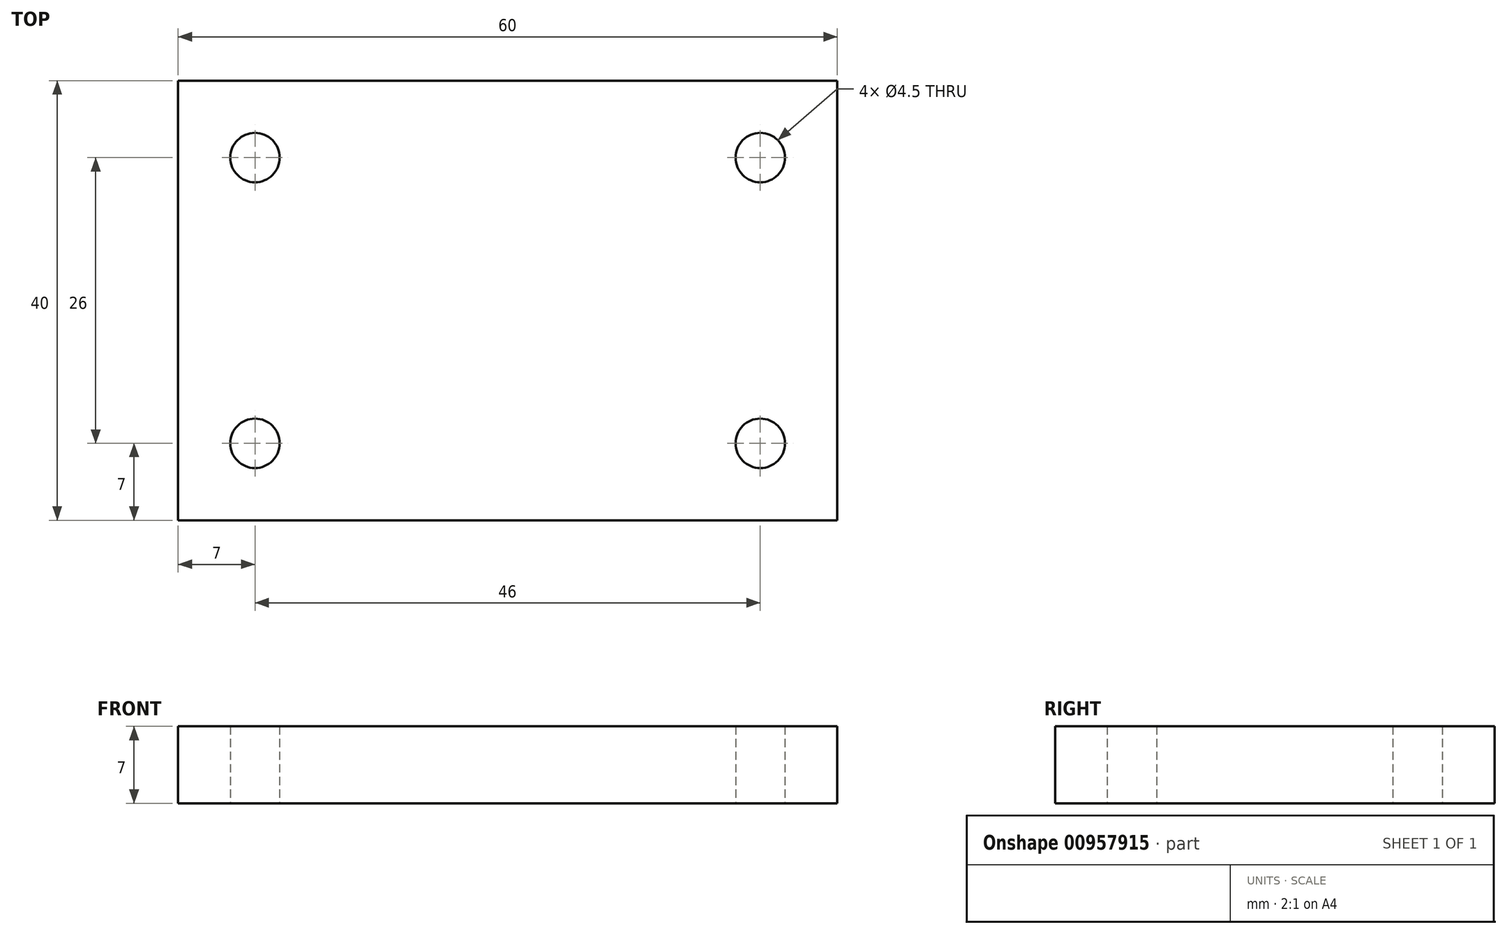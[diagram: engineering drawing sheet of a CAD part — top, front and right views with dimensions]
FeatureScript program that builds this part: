
annotation { "Feature Type Name" : "Feature", "Feature Type Description" : "" }
export const myFeature = defineFeature(function(context is Context, id is Id, definition is map)
    precondition{}
    {
        {
            var Q0;
            Q0=qCreatedBy(makeId("Top.planeOp"),FACE);
            var sketch = newSketch(context, id + "F0", { "sketchPlane" : qUnion([Q0])});
            skLineSegment(sketch, "E0.bottom", {"start": v(-30, 20) * mm, "end": v(30, 20) * mm});
            skLineSegment(sketch, "E0.top", {"start": v(-30, -20) * mm, "end": v(30, -20) * mm});
            skLineSegment(sketch, "E0.left", {"start": v(-30, 20) * mm, "end": v(-30, -20) * mm});
            skLineSegment(sketch, "E0.right", {"start": v(30, 20) * mm, "end": v(30, -20) * mm});
            skCircle(sketch, "E1", {"center": v(-23, 13) * mm, "radius": 2.25 * mm});
            skCircle(sketch, "E2.MirrorC", {"center": v(23, 13) * mm, "radius": 2.25 * mm});
            skCircle(sketch, "E3.MirrorC", {"center": v(-23, -13) * mm, "radius": 2.25 * mm});
            skCircle(sketch, "E4.MirrorC", {"center": v(23, -13) * mm, "radius": 2.25 * mm});
            skSolve(sketch);
        }
        {
            var Q0;
            Q0=makeQuery(id+"F0.imprint","IMPRINT",FACE,{"disambiguationData":[TD([[makeQuery(id+"F0.imprint","IMPRINT",EDGE,{"derivedFrom":sQuery(id+"F0.wireOp",EDGE,"E0.bottom")}),-1.0]])]});
            extrude(context, id + "F1", {"entities" : qUnion([Q0]), "depth" : 7 * mm, "offsetDistance" : 25 * mm});
        }
    });
